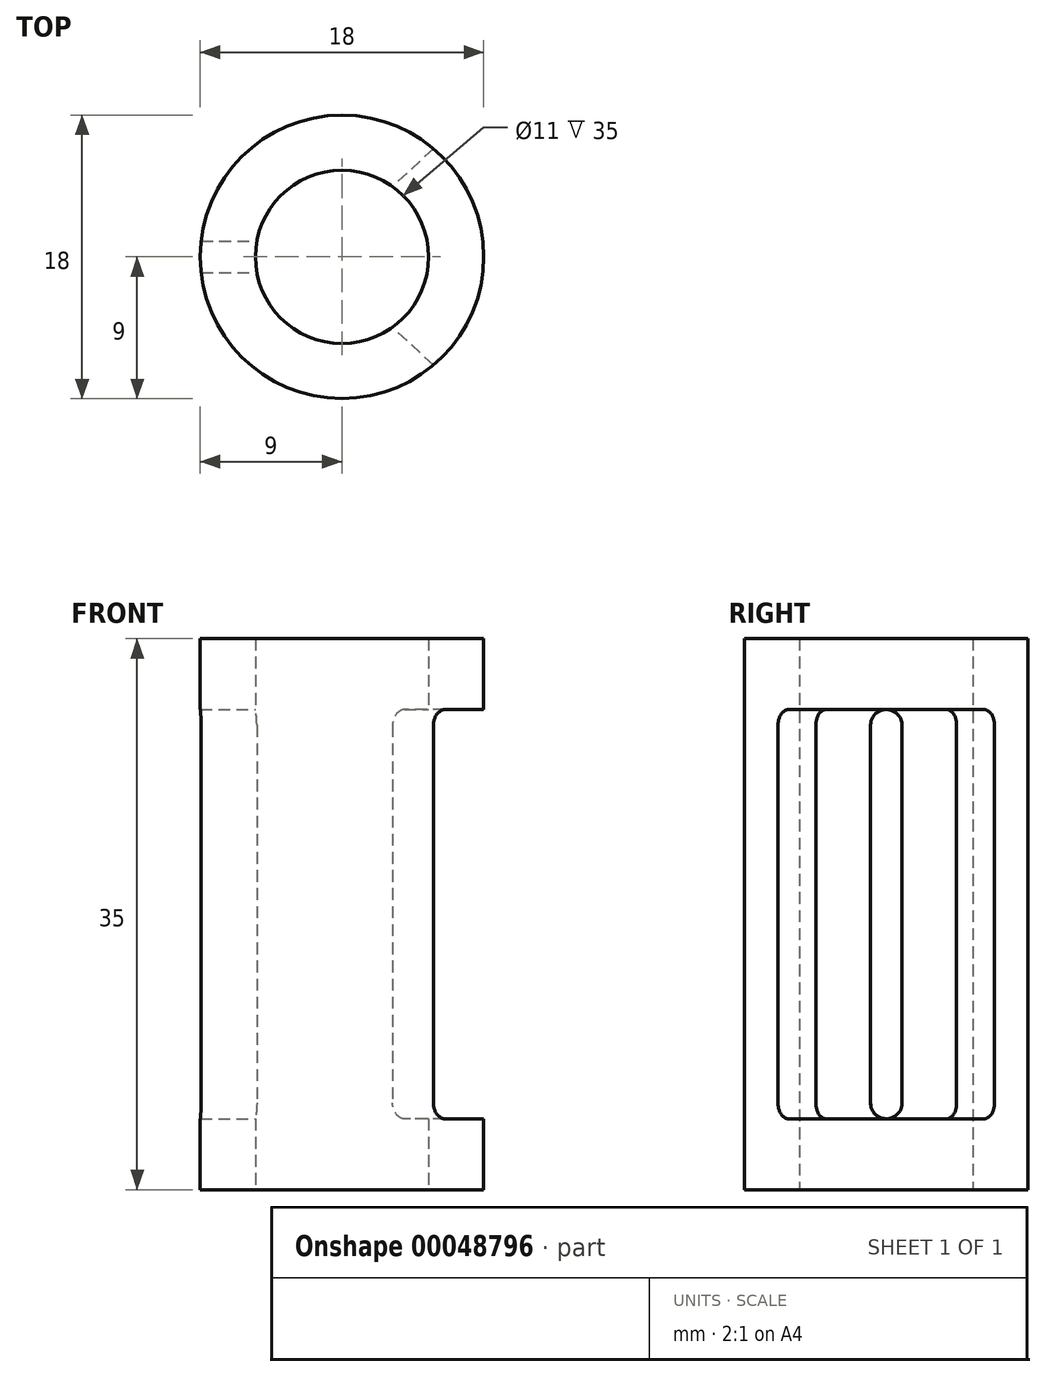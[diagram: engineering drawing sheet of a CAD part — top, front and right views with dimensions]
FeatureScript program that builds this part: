
annotation { "Feature Type Name" : "Feature", "Feature Type Description" : "" }
export const myFeature = defineFeature(function(context is Context, id is Id, definition is map)
    precondition{}
    {
        {
            var Q0;
            Q0=qCreatedBy(makeId("Top.planeOp"),FACE);
            var sketch = newSketch(context, id + "F0", { "sketchPlane" : qUnion([Q0])});
            skCircle(sketch, "E0", {"center": v(0, 0) * mm, "radius": 5.5 * mm});
            skCircle(sketch, "E1", {"center": v(0, 0) * mm, "radius": 9 * mm});
            skSolve(sketch);
        }
        {
            var Q0;
            Q0=makeQuery(id+"F0.imprint","IMPRINT",FACE,{"disambiguationData":[TD([[makeQuery(id+"F0.imprint","IMPRINT",EDGE,{"derivedFrom":sQuery(id+"F0.wireOp",EDGE,"E0")}),-1.0]])]});
            extrude(context, id + "F1", {"entities" : qUnion([Q0]), "depth" : 35 * mm});
        }
        {
            var Q0;
            Q0=qCreatedBy(makeId("Right.planeOp"),FACE);
            var sketch = newSketch(context, id + "F2", { "sketchPlane" : qUnion([Q0])});
            skPoint(sketch, "E2", {"position": v(0, 17.5) * mm});
            skLineSegment(sketch, "E3.bottom", {"start": v(0, 4.5) * mm, "end": v(0, 4.5) * mm});
            skLineSegment(sketch, "E3.top", {"start": v(0, 30.5) * mm, "end": v(0, 30.5) * mm});
            skLineSegment(sketch, "E3.left", {"start": v(1, 5.5) * mm, "end": v(1, 29.5) * mm});
            skLineSegment(sketch, "E3.right", {"start": v(-1, 5.5) * mm, "end": v(-1, 29.5) * mm});
            skPoint(sketch, "E4.visualSharp", {"position": v(-1, 30.5) * mm});
            skArc(sketch, "E4.filletArc", {"start": v(0, 30.5) * mm, "mid": v(-0.7, 30.2) * mm, "end": v(-1, 29.5) * mm});
            skPoint(sketch, "E5.visualSharp", {"position": v(1, 30.5) * mm});
            skArc(sketch, "E5.filletArc", {"start": v(1, 29.5) * mm, "mid": v(0.7, 30.2) * mm, "end": v(0, 30.5) * mm});
            skPoint(sketch, "E6.visualSharp", {"position": v(-1, 4.5) * mm});
            skArc(sketch, "E6.filletArc", {"start": v(-1, 5.5) * mm, "mid": v(-0.7, 4.8) * mm, "end": v(0, 4.5) * mm});
            skPoint(sketch, "E7.visualSharp", {"position": v(1, 4.5) * mm});
            skArc(sketch, "E7.filletArc", {"start": v(0, 4.5) * mm, "mid": v(0.7, 4.8) * mm, "end": v(1, 5.5) * mm});
            skSolve(sketch);
        }
        {
            var Q0;
            Q0 = qSketchRegion(id + "F2", true);
            extrude(context, id + "F3", {"entities" : qUnion([Q0]), "operationType" : NewBodyOperationType.REMOVE, "oppositeDirection" : true, "depth" : 25 * mm});
        }
        {
            var Q0;
            Q0=qCreatedBy(makeId("Right.planeOp"),FACE);
            var sketch = newSketch(context, id + "F4", { "sketchPlane" : qUnion([Q0])});
            skPoint(sketch, "E8", {"position": v(0, 17.5) * mm});
            skLineSegment(sketch, "E9.bottom", {"start": v(1.5, 4.5) * mm, "end": v(-1.5, 4.5) * mm});
            skLineSegment(sketch, "E9.top", {"start": v(1.5, 30.5) * mm, "end": v(-1.5, 30.5) * mm});
            skLineSegment(sketch, "E9.left", {"start": v(1.5, 4.5) * mm, "end": v(1.5, 30.5) * mm});
            skLineSegment(sketch, "E9.right", {"start": v(-1.5, 4.5) * mm, "end": v(-1.5, 30.5) * mm});
            skSolve(sketch);
        }
        {
            var Q0;
            Q0=qCreatedBy(makeId("Right.planeOp"),FACE);
            cPlane(context, id + "F5", {"entities" : qUnion([Q0]), "cplaneType" : CPlaneType.OFFSET, "offset" : 20 * mm, "width" : 150 * mm, "height" : 150 * mm});
        }
        {
            var Q0;
            Q0=qCreatedBy(id+"F5.planeOp",FACE);
            var sketch = newSketch(context, id + "F6", { "sketchPlane" : qUnion([Q0])});
            skPoint(sketch, "E10", {"position": v(0, 17.5) * mm});
            skLineSegment(sketch, "E11.bottom", {"start": v(20, 4.5) * mm, "end": v(-20, 4.5) * mm});
            skLineSegment(sketch, "E11.top", {"start": v(20, 30.5) * mm, "end": v(-20, 30.5) * mm});
            skLineSegment(sketch, "E11.left", {"start": v(20, 4.5) * mm, "end": v(20, 30.5) * mm});
            skLineSegment(sketch, "E11.right", {"start": v(-20, 4.5) * mm, "end": v(-20, 30.5) * mm});
            skSolve(sketch);
        }
        {
            var Q1;
            Q1=makeQuery(id+"F4.imprint","IMPRINT",FACE,{"disambiguationData":[TD([[makeQuery(id+"F4.imprint","IMPRINT",EDGE,{"derivedFrom":sQuery(id+"F4.wireOp",EDGE,"E9.bottom")}),-1.0]])]});
            var Q2;
            Q2=makeQuery(id+"F6.imprint","IMPRINT",FACE,{"disambiguationData":[TD([[makeQuery(id+"F6.imprint","IMPRINT",EDGE,{"derivedFrom":sQuery(id+"F6.wireOp",EDGE,"E11.bottom")}),-1.0]])]});
            loft(context, id + "F7", {"operationType" : NewBodyOperationType.REMOVE, "sheetProfilesArray" : [{ "sheetProfileEntities" : qUnion([Q1]) }, { "sheetProfileEntities" : qUnion([Q2]) }]});
        }
        {
            var Q0;
            Q0=makeQuery(id+"F7.boolean.opBoolean","COPY",EDGE,{"derivedFrom":makeQuery(id+"F7.opLoft","SWEPT_EDGE",EDGE,{"disambiguationData":[OSD([sQuery(id+"F4.wireOp",EDGE,"E9.top"),sQuery(id+"F4.wireOp",EDGE,"E9.right"),sQuery(id+"F6.wireOp",EDGE,"E11.top"),sQuery(id+"F6.wireOp",EDGE,"E11.right")])]})});
            var Q1;
            Q1=makeQuery(id+"F7.boolean.opBoolean","COPY",EDGE,{"derivedFrom":makeQuery(id+"F7.opLoft","SWEPT_EDGE",EDGE,{"disambiguationData":[OSD([sQuery(id+"F4.wireOp",EDGE,"E9.top"),sQuery(id+"F4.wireOp",EDGE,"E9.left"),sQuery(id+"F6.wireOp",EDGE,"E11.top"),sQuery(id+"F6.wireOp",EDGE,"E11.left")])]})});
            var Q2;
            Q2=makeQuery(id+"F7.boolean.opBoolean","COPY",EDGE,{"derivedFrom":makeQuery(id+"F7.opLoft","SWEPT_EDGE",EDGE,{"disambiguationData":[OSD([sQuery(id+"F4.wireOp",EDGE,"E9.bottom"),sQuery(id+"F4.wireOp",EDGE,"E9.left"),sQuery(id+"F6.wireOp",EDGE,"E11.bottom"),sQuery(id+"F6.wireOp",EDGE,"E11.left")])]})});
            var Q3;
            Q3=makeQuery(id+"F7.boolean.opBoolean","COPY",EDGE,{"derivedFrom":makeQuery(id+"F7.opLoft","SWEPT_EDGE",EDGE,{"disambiguationData":[OSD([sQuery(id+"F4.wireOp",EDGE,"E9.bottom"),sQuery(id+"F4.wireOp",EDGE,"E9.right"),sQuery(id+"F6.wireOp",EDGE,"E11.bottom"),sQuery(id+"F6.wireOp",EDGE,"E11.right")])]})});
            fillet(context, id + "F8", {"entities" : qUnion([Q0, Q1, Q2, Q3]), "radius" : 1 * mm, "tangentPropagation" : true, "allowEdgeOverflow" : false});
        }
    });
